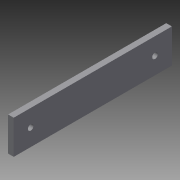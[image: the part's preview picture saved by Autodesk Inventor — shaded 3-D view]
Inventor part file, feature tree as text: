
AUTODESK INVENTOR PART (.ipt)
format: ipt  version: 2015 (Build 190159000, 159)  size: 77,312 bytes
history: native  units: in
note: dims shown in document units (in); Inventor stores cm internally (conversion verified against a paired STEP export)
features: extrude x1, sketch x1
ambient origin geometry x8: Origin, YZ Plane, XZ Plane, XY Plane, X Axis, Y Axis, Z Axis, Center Point
bodies: Solid1 (feature_tree)
feature tree (2):
  extrude  "Extrusion1"  Depth=9.0in
  sketch  "Sketch1"  dims[d0=1.5in d1=9.0in d2=0.75in d3=0.75in d4=0.75in d5=0.75in d6=0.25in d7=0.25in d8=0.25in d9=0.0in]
